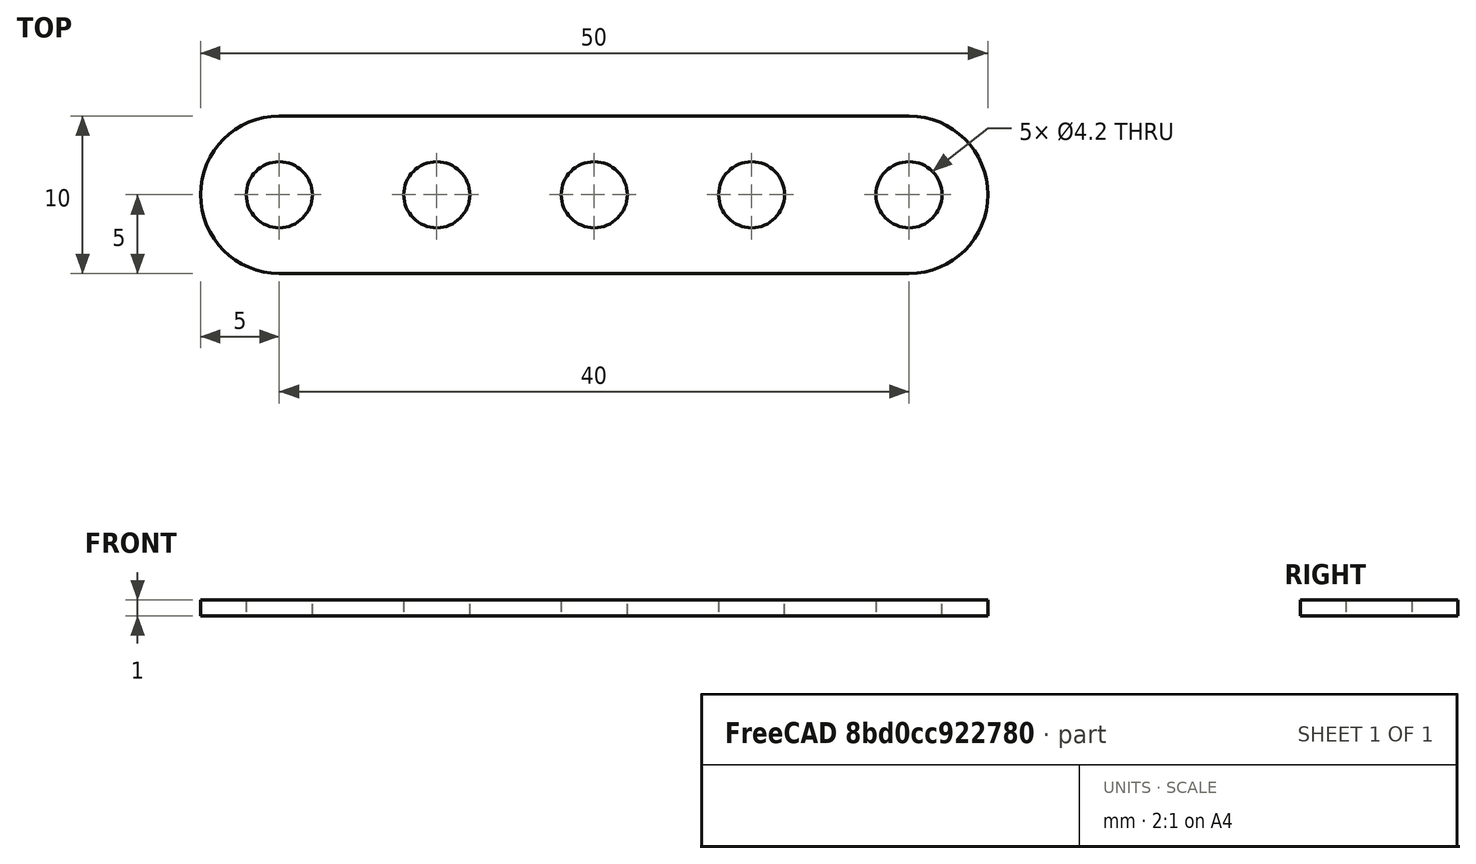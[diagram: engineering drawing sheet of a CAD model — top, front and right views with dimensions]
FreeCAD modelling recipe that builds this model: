
FCSTD DOCUMENT  (FreeCAD 0.16RUnknown)
Label: strip_1x5
License: All rights reserved
LicenseURL: http://en.wikipedia.org/wiki/All_rights_reserved
objects: Drawing::FeatureViewPart×2, Sketcher::SketchObject×1, PartDesign::Pad×1, Drawing::FeaturePage×1
note: 3 computed .brp shape members not serialized (recipe doc carries the construction recipe); baked Part::Feature solids carry a one-line shape summary decoded from their .brp

FEATURE [Sketcher::SketchObject] Sketch
  sketch-geometry (13):
    g0: Circle CenterX=0 CenterY=0 CenterZ=0 NormalX=0 NormalY=0 NormalZ=1 Radius=2.1
    g1: Circle CenterX=10 CenterY=0 CenterZ=0 NormalX=0 NormalY=0 NormalZ=1 Radius=2.1
    g2: LineSegment [constr] StartX=0 StartY=0 StartZ=0 EndX=10 EndY=0 EndZ=0
    g3: Circle CenterX=20 CenterY=0 CenterZ=0 NormalX=0 NormalY=0 NormalZ=1 Radius=2.1
    g4: LineSegment [constr] StartX=10 StartY=0 StartZ=0 EndX=20 EndY=0 EndZ=0
    g5: Circle CenterX=30 CenterY=0 CenterZ=0 NormalX=0 NormalY=0 NormalZ=1 Radius=2.1
    g6: LineSegment [constr] StartX=20 StartY=0 StartZ=0 EndX=30 EndY=0 EndZ=0
    g7: Circle CenterX=40 CenterY=0 CenterZ=0 NormalX=0 NormalY=0 NormalZ=1 Radius=2.1
    g8: LineSegment [constr] StartX=30 StartY=0 StartZ=0 EndX=40 EndY=0 EndZ=0
    g9: ArcOfCircle CenterX=0 CenterY=0 CenterZ=0 NormalX=0 NormalY=0 NormalZ=1 Radius=5 StartAngle=1.5708 EndAngle=4.71239
    g10: ArcOfCircle CenterX=40 CenterY=0 CenterZ=0 NormalX=0 NormalY=0 NormalZ=1 Radius=5 StartAngle=4.71239 EndAngle=7.85398
    g11: LineSegment StartX=0 StartY=-5 StartZ=0 EndX=40 EndY=-5 EndZ=0
    g12: LineSegment StartX=0 StartY=5 StartZ=0 EndX=40 EndY=5 EndZ=0
  constraints (31):
    c: Radius(g0) = 2.1
    c: Equal(g0,g1) = 5
    c: Coincident(g0,g2)
    c: Coincident(g1,g2)
    c: Equal(g0,g3) = 5
    c: Coincident(g1,g4)
    c: Coincident(g3,g4)
    c: Equal(g2,g4)
    c: Parallel(g4,g2)
    c: Equal(g0,g5) = 5
    c: Coincident(g3,g6)
    c: Coincident(g5,g6)
    c: Equal(g2,g6)
    c: Parallel(g6,g2)
    c: Equal(g0,g7) = 5
    c: Coincident(g5,g8)
    c: Coincident(g7,g8)
    c: Equal(g2,g8)
    c: Parallel(g8,g2)
    c: Coincident(g0,g-1)
    c: Distance(g-1,g1) = 10
    c: Angle(g2,g-1) = 0
    c: Tangent(g9,g12) = 1.5708
    c: Tangent(g9,g11) = -1.5708
    c: Tangent(g11,g10) = -1.5708
    c: Tangent(g12,g10) = 1.5708
    c: Horizontal(g11)
    c: Equal(g9,g10)
    c: Coincident(g-1,g9)
    c: Radius(g9) = 5
    c: Coincident(g10,g7)
FEATURE [PartDesign::Pad] Pad
  Length = 1
  Length2 = 100
  Sketch = -> Sketch
  Type = 0
FEATURE [Drawing::FeatureViewPart] Ortho  label="Ortho_0_0"
  Direction = (1,0,0)
  HiddenWidth = 0.15
  LineWidth = 0.35
  Rotation = -90
  ShowHiddenLines = false
  ShowSmoothLines = false
  Source = -> Pad
  Tolerance = 0.05
  ViewResult = <g id="Ortho_0_0"\n   transform="rotate(-90,105,264.5) translate(105,264.5) scale(1,1)"\n  >\n<g   stroke="rgb(0, 0, 0)"\n   stroke-width="0.35"\n   stroke-linecap="butt"\n   stroke-linejoin="miter"\n   fill="none"\n   transform="scale(1,-1)"\n  >\n<path id= "1" d=" M 0 5 L 1 5 " />\n<path id= "2" d=" M 0 -5 L 1 -5 " />\n<path d="M0,5 L0,4.87464  L0,4.50484  L0,3.90916  L0,3.11745  L0,2.16942  L0,1.1126  L0,1.48111e-15  L0,-1.1126  L0,-2.16942  L0,-3.11745  L0,-3.90916  L0,-4.50484  L0,-4.87464  L0,-5 " /><path d="M1,5 L1,4.87464  L1,4.50484  L1,3.90916  L1,3.11745  L1,2.16942  L1,1.1126  L1,1.48111e-15  L1,-1.1126  L1,-2.16942  L1,-3.11745  L1,-3.90916  L1,-4.50484  L1,-4.87464  L1,-5 " /></g>\n</g>
  Visible = true
  X = 105
  Y = 264.5
FEATURE [Drawing::FeatureViewPart] Ortho001  label="Ortho_0_1"
  Direction = (0,0,1)
  HiddenWidth = 0.15
  LineWidth = 0.35
  Rotation = 90
  ShowHiddenLines = false
  ShowSmoothLines = false
  Source = -> Pad
  Tolerance = 0.05
  ViewResult = <g id="Ortho_0_1"\n   transform="rotate(90,105,111) translate(105,111) scale(1,1)"\n  >\n<g   stroke="rgb(0, 0, 0)"\n   stroke-width="0.35"\n   stroke-linecap="butt"\n   stroke-linejoin="miter"\n   fill="none"\n   transform="scale(1,-1)"\n  >\n<path d="M-1.74574e-14 5 A5 5 0 0 1 -9.18485e-16 -5" /><path id= "2" d=" M -9.18485e-16 -5 L 40 -5 " />\n<path d="M40 -5 A5 5 0 0 1 40 5" /><path id= "4" d=" M -2.48186e-15 5 L 40 5 " />\n<circle cx ="10" cy ="0" r ="2.1" /><circle cx ="0" cy ="0" r ="2.1" /><circle cx ="40" cy ="0" r ="2.1" /><circle cx ="30" cy ="0" r ="2.1" /><circle cx ="20" cy ="0" r ="2.1" /></g>\n</g>
  Visible = true
  X = 105
  Y = 111
FEATURE [Drawing::FeaturePage] Page
  Group = -> [Ortho,Ortho001]
